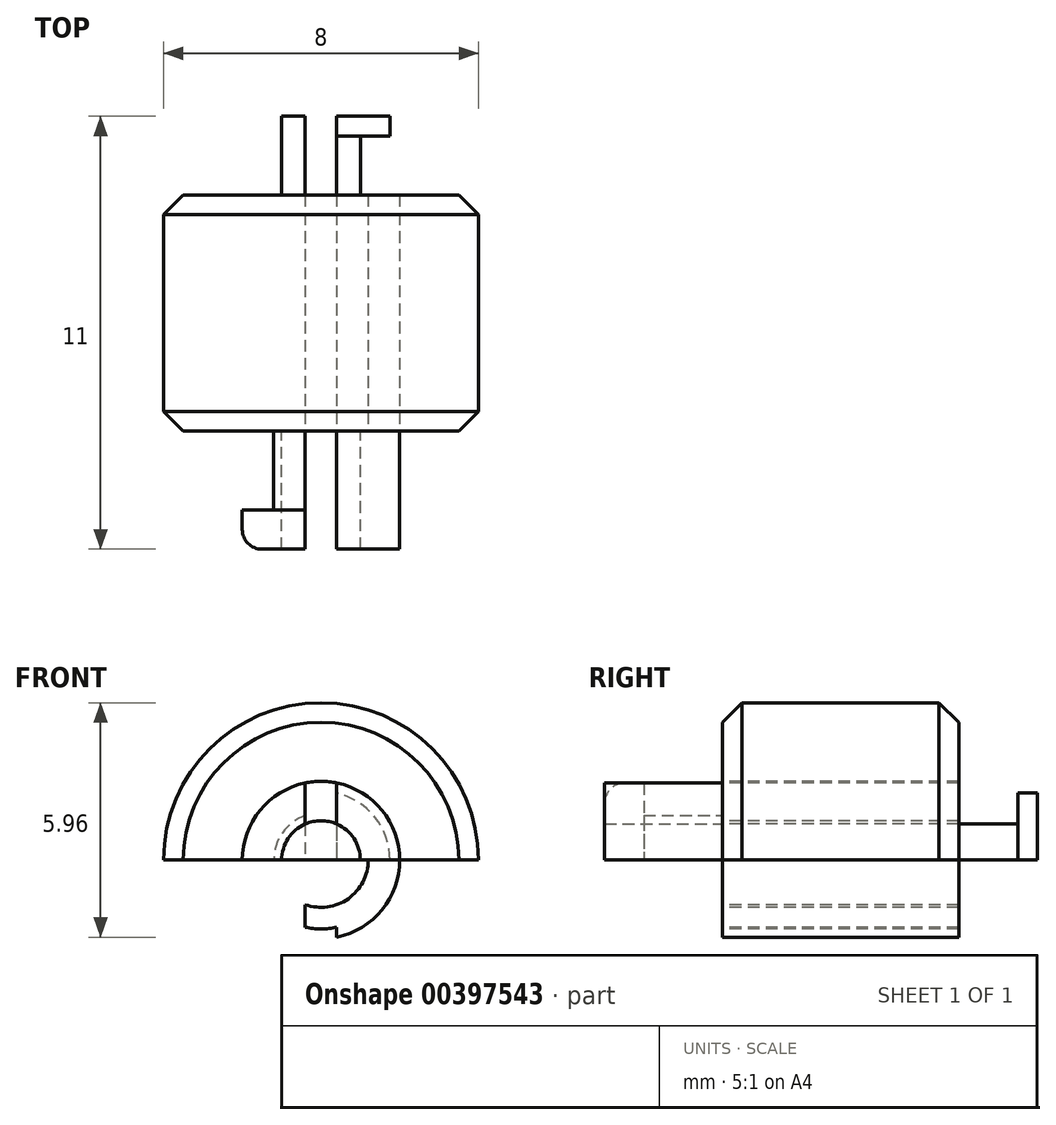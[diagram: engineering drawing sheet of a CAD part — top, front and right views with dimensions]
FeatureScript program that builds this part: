
annotation { "Feature Type Name" : "Feature", "Feature Type Description" : "" }
export const myFeature = defineFeature(function(context is Context, id is Id, definition is map)
    precondition{}
    {
        {
            var Q0;
            Q0=qCreatedBy(makeId("Front.planeOp"),FACE);
            var sketch = newSketch(context, id + "F0", { "sketchPlane" : qUnion([Q0])});
            skCircle(sketch, "E0", {"center": v(0, 0) * mm, "radius": 4 * mm});
            skLineSegment(sketch, "E1", {"start": v(-4, 0) * mm, "end": v(4, 0) * mm});
            skCircle(sketch, "E2", {"center": v(0, 0) * mm, "radius": 1.75 * mm});
            skLineSegment(sketch, "E3.bottom", {"start": v(0.4, 2) * mm, "end": v(-0.4, 2) * mm});
            skLineSegment(sketch, "E3.top", {"start": v(0.4, -2) * mm, "end": v(-0.4, -2) * mm});
            skLineSegment(sketch, "E3.left", {"start": v(0.4, 2) * mm, "end": v(0.4, -2) * mm});
            skLineSegment(sketch, "E3.right", {"start": v(-0.4, 2) * mm, "end": v(-0.4, -2) * mm});
            skCircle(sketch, "E4", {"center": v(0, 0) * mm, "radius": 2 * mm});
            skCircle(sketch, "E5", {"center": v(0, 0) * mm, "radius": 1 * mm});
            skCircle(sketch, "E6.0", {"center": v(0, 0) * mm, "radius": 1.2 * mm});
            skSolve(sketch);
        }
        {
            var Q0;
            {var subQ0=sQuery(id+"F0.wireOp",EDGE,"E1");var subQ1=sQuery(id+"F0.wireOp",EDGE,"E0");var subQ9=makeQuery(id+"F0.imprint","INTERSECT",VERTEX,{"disambiguationData":[OD(0.0)],"derivedFrom":[subQ1,subQ0]});Q0=makeQuery(id+"F0.imprint","IMPRINT",FACE,{"disambiguationData":[TD([[makeQuery(id+"F0.imprint","IMPRINT",EDGE,{"disambiguationData":[TD([[subQ9,1.0]])],"derivedFrom":subQ1}),1.0]])]});}
            var Q1;
            {var subQ0=sQuery(id+"F0.wireOp",EDGE,"E2");var subQ1=sQuery(id+"F0.wireOp",EDGE,"E1");var subQ2=makeQuery(id+"F0.imprint","INTERSECT",VERTEX,{"disambiguationData":[OD(1.0)],"derivedFrom":[subQ1,subQ0]});Q1=makeQuery(id+"F0.imprint","IMPRINT",FACE,{"disambiguationData":[TD([[makeQuery(id+"F0.imprint","IMPRINT",EDGE,{"disambiguationData":[TD([[subQ2,-1.0]])],"derivedFrom":subQ1}),1.0]])]});}
            var Q2;
            {var subQ2=sQuery(id+"F0.wireOp",EDGE,"E3.left");var subQ4=sQuery(id+"F0.wireOp",EDGE,"E2");var subQ5=makeQuery(id+"F0.imprint","INTERSECT",VERTEX,{"disambiguationData":[OD(0.0)],"derivedFrom":[subQ4,subQ2]});Q2=makeQuery(id+"F0.imprint","IMPRINT",FACE,{"disambiguationData":[TD([[makeQuery(id+"F0.imprint","IMPRINT",EDGE,{"disambiguationData":[TD([[subQ5,-1.0]])],"derivedFrom":subQ4}),-1.0]])]});}
            var Q3;
            {var subQ0=sQuery(id+"F0.wireOp",EDGE,"E2");var subQ1=sQuery(id+"F0.wireOp",EDGE,"E1");var subQ2=makeQuery(id+"F0.imprint","INTERSECT",VERTEX,{"disambiguationData":[OD(0.0)],"derivedFrom":[subQ1,subQ0]});Q3=makeQuery(id+"F0.imprint","IMPRINT",FACE,{"disambiguationData":[TD([[makeQuery(id+"F0.imprint","IMPRINT",EDGE,{"disambiguationData":[TD([[subQ2,-1.0]])],"derivedFrom":subQ1}),1.0]])]});}
            var Q4;
            {var subQ0=sQuery(id+"F0.wireOp",EDGE,"E4");var subQ1=sQuery(id+"F0.wireOp",EDGE,"E1");var subQ2=makeQuery(id+"F0.imprint","INTERSECT",VERTEX,{"disambiguationData":[OD(0.0)],"derivedFrom":[subQ1,subQ0]});Q4=makeQuery(id+"F0.imprint","IMPRINT",FACE,{"disambiguationData":[TD([[makeQuery(id+"F0.imprint","IMPRINT",EDGE,{"disambiguationData":[TD([[subQ2,-1.0]])],"derivedFrom":subQ1}),1.0]])]});}
            var Q5;
            {var subQ0=sQuery(id+"F0.wireOp",EDGE,"E3.left");var subQ1=sQuery(id+"F0.wireOp",EDGE,"E3.bottom");var subQ2=makeQuery(id+"F0.imprint","INTERSECT",VERTEX,{"derivedFrom":[subQ1,subQ0]});Q5=makeQuery(id+"F0.imprint","IMPRINT",FACE,{"disambiguationData":[TD([[makeQuery(id+"F0.imprint","IMPRINT",EDGE,{"disambiguationData":[TD([[subQ2,-1.0]])],"derivedFrom":subQ1}),1.0]])]});}
            var Q6;
            {var subQ0=sQuery(id+"F0.wireOp",EDGE,"E3.right");var subQ1=sQuery(id+"F0.wireOp",EDGE,"E3.bottom");var subQ2=makeQuery(id+"F0.imprint","INTERSECT",VERTEX,{"derivedFrom":[subQ1,subQ0]});Q6=makeQuery(id+"F0.imprint","IMPRINT",FACE,{"disambiguationData":[TD([[makeQuery(id+"F0.imprint","IMPRINT",EDGE,{"disambiguationData":[TD([[subQ2,1.0]])],"derivedFrom":subQ1}),1.0]])]});}
            var Q7;
            {var subQ0=sQuery(id+"F0.wireOp",EDGE,"E5");var subQ1=sQuery(id+"F0.wireOp",EDGE,"E1");var subQ2=makeQuery(id+"F0.imprint","INTERSECT",VERTEX,{"disambiguationData":[OD(1.0)],"derivedFrom":[subQ1,subQ0]});Q7=makeQuery(id+"F0.imprint","IMPRINT",FACE,{"disambiguationData":[TD([[makeQuery(id+"F0.imprint","IMPRINT",EDGE,{"disambiguationData":[TD([[subQ2,-1.0]])],"derivedFrom":subQ1}),1.0]])]});}
            var Q8;
            {var subQ0=sQuery(id+"F0.wireOp",EDGE,"E3.left");var subQ1=sQuery(id+"F0.wireOp",EDGE,"E2");var subQ2=makeQuery(id+"F0.imprint","INTERSECT",VERTEX,{"disambiguationData":[OD(0.0)],"derivedFrom":[subQ1,subQ0]});Q8=makeQuery(id+"F0.imprint","IMPRINT",FACE,{"disambiguationData":[TD([[makeQuery(id+"F0.imprint","IMPRINT",EDGE,{"disambiguationData":[TD([[subQ2,-1.0]])],"derivedFrom":subQ1}),1.0]])]});}
            var Q9;
            {var subQ0=sQuery(id+"F0.wireOp",EDGE,"E6.0");var subQ1=sQuery(id+"F0.wireOp",EDGE,"E1");var subQ2=makeQuery(id+"F0.imprint","INTERSECT",VERTEX,{"disambiguationData":[OD(1.0)],"derivedFrom":[subQ1,subQ0]});Q9=makeQuery(id+"F0.imprint","IMPRINT",FACE,{"disambiguationData":[TD([[makeQuery(id+"F0.imprint","IMPRINT",EDGE,{"disambiguationData":[TD([[subQ2,-1.0]])],"derivedFrom":subQ1}),1.0]])]});}
            var Q10;
            {var subQ0=sQuery(id+"F0.wireOp",EDGE,"E6.0");var subQ1=sQuery(id+"F0.wireOp",EDGE,"E3.left");var subQ2=makeQuery(id+"F0.imprint","INTERSECT",VERTEX,{"disambiguationData":[OD(0.0)],"derivedFrom":[subQ1,subQ0]});Q10=makeQuery(id+"F0.imprint","IMPRINT",FACE,{"disambiguationData":[TD([[makeQuery(id+"F0.imprint","IMPRINT",EDGE,{"disambiguationData":[TD([[subQ2,-1.0]])],"derivedFrom":subQ1}),-1.0]])]});}
            var Q11;
            {var subQ0=sQuery(id+"F0.wireOp",EDGE,"E6.0");var subQ1=sQuery(id+"F0.wireOp",EDGE,"E1");var subQ2=makeQuery(id+"F0.imprint","INTERSECT",VERTEX,{"disambiguationData":[OD(0.0)],"derivedFrom":[subQ1,subQ0]});Q11=makeQuery(id+"F0.imprint","IMPRINT",FACE,{"disambiguationData":[TD([[makeQuery(id+"F0.imprint","IMPRINT",EDGE,{"disambiguationData":[TD([[subQ2,-1.0]])],"derivedFrom":subQ1}),1.0]])]});}
            var Q12;
            {var subQ0=sQuery(id+"F0.wireOp",EDGE,"E3.left");var subQ1=sQuery(id+"F0.wireOp",EDGE,"E1");var subQ2=makeQuery(id+"F0.imprint","INTERSECT",VERTEX,{"derivedFrom":[subQ1,subQ0]});Q12=makeQuery(id+"F0.imprint","IMPRINT",FACE,{"disambiguationData":[TD([[makeQuery(id+"F0.imprint","IMPRINT",EDGE,{"disambiguationData":[TD([[subQ2,-1.0]])],"derivedFrom":subQ1}),1.0]])]});}
            var Q13;
            {var subQ0=sQuery(id+"F0.wireOp",EDGE,"E3.right");var subQ1=sQuery(id+"F0.wireOp",EDGE,"E1");var subQ2=makeQuery(id+"F0.imprint","INTERSECT",VERTEX,{"derivedFrom":[subQ1,subQ0]});Q13=makeQuery(id+"F0.imprint","IMPRINT",FACE,{"disambiguationData":[TD([[makeQuery(id+"F0.imprint","IMPRINT",EDGE,{"disambiguationData":[TD([[subQ2,-1.0]])],"derivedFrom":subQ1}),1.0]])]});}
            var Q14;
            {var subQ0=sQuery(id+"F0.wireOp",EDGE,"E5");var subQ1=sQuery(id+"F0.wireOp",EDGE,"E1");var subQ2=makeQuery(id+"F0.imprint","INTERSECT",VERTEX,{"disambiguationData":[OD(0.0)],"derivedFrom":[subQ1,subQ0]});Q14=makeQuery(id+"F0.imprint","IMPRINT",FACE,{"disambiguationData":[TD([[makeQuery(id+"F0.imprint","IMPRINT",EDGE,{"disambiguationData":[TD([[subQ2,-1.0]])],"derivedFrom":subQ1}),1.0]])]});}
            extrude(context, id + "F1", {"entities" : qUnion([Q0, Q1, Q2, Q3, Q4, Q5, Q6, Q7, Q8, Q9, Q10, Q11, Q12, Q13, Q14]), "oppositeDirection" : true, "depth" : 6 * mm});
        }
        {
            var Q0;
            {var subQ0=sQuery(id+"F0.wireOp",EDGE,"E2");var subQ1=sQuery(id+"F0.wireOp",EDGE,"E1");var subQ2=makeQuery(id+"F0.imprint","INTERSECT",VERTEX,{"disambiguationData":[OD(0.0)],"derivedFrom":[subQ1,subQ0]});Q0=makeQuery(id+"F0.imprint","IMPRINT",FACE,{"disambiguationData":[TD([[makeQuery(id+"F0.imprint","IMPRINT",EDGE,{"disambiguationData":[TD([[subQ2,-1.0]])],"derivedFrom":subQ1}),1.0]])]});}
            var Q1;
            {var subQ0=sQuery(id+"F0.wireOp",EDGE,"E5");var subQ1=sQuery(id+"F0.wireOp",EDGE,"E1");var subQ2=makeQuery(id+"F0.imprint","INTERSECT",VERTEX,{"disambiguationData":[OD(1.0)],"derivedFrom":[subQ1,subQ0]});Q1=makeQuery(id+"F0.imprint","IMPRINT",FACE,{"disambiguationData":[TD([[makeQuery(id+"F0.imprint","IMPRINT",EDGE,{"disambiguationData":[TD([[subQ2,-1.0]])],"derivedFrom":subQ1}),1.0]])]});}
            var Q2;
            {var subQ0=sQuery(id+"F0.wireOp",EDGE,"E6.0");var subQ1=sQuery(id+"F0.wireOp",EDGE,"E1");var subQ2=makeQuery(id+"F0.imprint","INTERSECT",VERTEX,{"disambiguationData":[OD(1.0)],"derivedFrom":[subQ1,subQ0]});Q2=makeQuery(id+"F0.imprint","IMPRINT",FACE,{"disambiguationData":[TD([[makeQuery(id+"F0.imprint","IMPRINT",EDGE,{"disambiguationData":[TD([[subQ2,-1.0]])],"derivedFrom":subQ1}),1.0]])]});}
            var Q3;
            {var subQ0=sQuery(id+"F0.wireOp",EDGE,"E6.0");var subQ1=sQuery(id+"F0.wireOp",EDGE,"E1");var subQ2=makeQuery(id+"F0.imprint","INTERSECT",VERTEX,{"disambiguationData":[OD(0.0)],"derivedFrom":[subQ1,subQ0]});Q3=makeQuery(id+"F0.imprint","IMPRINT",FACE,{"disambiguationData":[TD([[makeQuery(id+"F0.imprint","IMPRINT",EDGE,{"disambiguationData":[TD([[subQ2,-1.0]])],"derivedFrom":subQ1}),1.0]])]});}
            extrude(context, id + "F2", {"entities" : qUnion([Q0, Q1, Q2, Q3]), "operationType" : NewBodyOperationType.ADD, "depth" : 3 * mm});
        }
        {
            var Q0;
            {var subQ0=sQuery(id+"F0.wireOp",EDGE,"E2");var subQ1=sQuery(id+"F0.wireOp",EDGE,"E1");var subQ2=makeQuery(id+"F0.imprint","INTERSECT",VERTEX,{"disambiguationData":[OD(1.0)],"derivedFrom":[subQ1,subQ0]});Q0=makeQuery(id+"F0.imprint","IMPRINT",FACE,{"disambiguationData":[TD([[makeQuery(id+"F0.imprint","IMPRINT",EDGE,{"disambiguationData":[TD([[subQ2,-1.0]])],"derivedFrom":subQ1}),1.0]])]});}
            var Q1;
            {var subQ0=sQuery(id+"F0.wireOp",EDGE,"E4");var subQ1=sQuery(id+"F0.wireOp",EDGE,"E1");var subQ2=makeQuery(id+"F0.imprint","INTERSECT",VERTEX,{"disambiguationData":[OD(0.0)],"derivedFrom":[subQ1,subQ0]});Q1=makeQuery(id+"F0.imprint","IMPRINT",FACE,{"disambiguationData":[TD([[makeQuery(id+"F0.imprint","IMPRINT",EDGE,{"disambiguationData":[TD([[subQ2,-1.0]])],"derivedFrom":subQ1}),1.0]])]});}
            extrude(context, id + "F3", {"entities" : qUnion([Q0, Q1]), "operationType" : NewBodyOperationType.ADD, "depth" : 3 * mm, "hasSecondDirection" : true, "secondDirectionOppositeDirection" : false, "secondDirectionDepth" : 2 * mm});
        }
        {
            var Q0;
            Q0=makeQuery(id+"F1.opExtrude","CAP_EDGE",EDGE,{"disambiguationData":[OSD([sQuery(id+"F0.wireOp",EDGE,"E0")])],"isStart":true});
            var Q1;
            Q1=makeQuery(id+"F1.opExtrude","CAP_EDGE",EDGE,{"disambiguationData":[OSD([sQuery(id+"F0.wireOp",EDGE,"E0")])],"isStart":false});
            chamfer(context, id + "F4", {"entities" : qUnion([Q0, Q1]), "width" : 0.5 * mm, "tangentPropagation" : true});
        }
        {
            var Q0;
            {var subQ0=sQuery(id+"F0.wireOp",EDGE,"E3.left");var subQ1=sQuery(id+"F0.wireOp",EDGE,"E1");var subQ2=makeQuery(id+"F0.imprint","INTERSECT",VERTEX,{"derivedFrom":[subQ1,subQ0]});Q0=makeQuery(id+"F0.imprint","IMPRINT",FACE,{"disambiguationData":[TD([[makeQuery(id+"F0.imprint","IMPRINT",EDGE,{"disambiguationData":[TD([[subQ2,-1.0]])],"derivedFrom":subQ1}),1.0]])]});}
            var Q1;
            {var subQ0=sQuery(id+"F0.wireOp",EDGE,"E5");var subQ1=sQuery(id+"F0.wireOp",EDGE,"E1");var subQ2=makeQuery(id+"F0.imprint","INTERSECT",VERTEX,{"disambiguationData":[OD(0.0)],"derivedFrom":[subQ1,subQ0]});Q1=makeQuery(id+"F0.imprint","IMPRINT",FACE,{"disambiguationData":[TD([[makeQuery(id+"F0.imprint","IMPRINT",EDGE,{"disambiguationData":[TD([[subQ2,-1.0]])],"derivedFrom":subQ1}),1.0]])]});}
            extrude(context, id + "F5", {"entities" : qUnion([Q0, Q1]), "operationType" : NewBodyOperationType.ADD, "oppositeDirection" : true, "depth" : 8 * mm});
        }
        {
            var Q0;
            {var subQ0=sQuery(id+"F0.wireOp",EDGE,"E6.0");var subQ1=sQuery(id+"F0.wireOp",EDGE,"E1");var subQ2=makeQuery(id+"F0.imprint","INTERSECT",VERTEX,{"disambiguationData":[OD(0.0)],"derivedFrom":[subQ1,subQ0]});Q0=makeQuery(id+"F0.imprint","IMPRINT",FACE,{"disambiguationData":[TD([[makeQuery(id+"F0.imprint","IMPRINT",EDGE,{"disambiguationData":[TD([[subQ2,-1.0]])],"derivedFrom":subQ1}),1.0]])]});}
            var Q1;
            {var subQ0=sQuery(id+"F0.wireOp",EDGE,"E5");var subQ1=sQuery(id+"F0.wireOp",EDGE,"E1");var subQ2=makeQuery(id+"F0.imprint","INTERSECT",VERTEX,{"disambiguationData":[OD(1.0)],"derivedFrom":[subQ1,subQ0]});Q1=makeQuery(id+"F0.imprint","IMPRINT",FACE,{"disambiguationData":[TD([[makeQuery(id+"F0.imprint","IMPRINT",EDGE,{"disambiguationData":[TD([[subQ2,-1.0]])],"derivedFrom":subQ1}),1.0]])]});}
            extrude(context, id + "F6", {"entities" : qUnion([Q0, Q1]), "operationType" : NewBodyOperationType.ADD, "oppositeDirection" : true, "depth" : 8 * mm, "hasSecondDirection" : true, "secondDirectionOppositeDirection" : true, "secondDirectionDepth" : 7.5 * mm});
        }
        {
            var Q0;
            {var subQ0=sQuery(id+"F0.wireOp",EDGE,"E6.0");Q0=makeQuery(id+"F6.opExtrude","CAP_EDGE",EDGE,{"disambiguationData":[OSD([subQ0]),TDD([makeQuery(id+"F0.imprint","IMPRINT",EDGE,{"disambiguationData":[TD([[makeQuery(id+"F0.imprint","INTERSECT",VERTEX,{"disambiguationData":[OD(1.0)],"derivedFrom":[sQuery(id+"F0.wireOp",EDGE,"E1"),subQ0]}),-1.0]])],"derivedFrom":subQ0})])],"isStart":false});}
            var Q1;
            {var subQ0=sQuery(id+"F0.wireOp",EDGE,"E6.0");Q1=makeQuery(id+"F6.opExtrude","CAP_EDGE",EDGE,{"disambiguationData":[OSD([subQ0]),TDD([makeQuery(id+"F0.imprint","IMPRINT",EDGE,{"disambiguationData":[TD([[makeQuery(id+"F0.imprint","INTERSECT",VERTEX,{"disambiguationData":[OD(0.0)],"derivedFrom":[sQuery(id+"F0.wireOp",EDGE,"E1"),subQ0]}),1.0]])],"derivedFrom":subQ0})])],"isStart":false});}
            var Q2;
            {var subQ0=sQuery(id+"F0.wireOp",EDGE,"E4");Q2=makeQuery(id+"F3.opExtrude","CAP_EDGE",EDGE,{"disambiguationData":[OSD([subQ0]),TDD([makeQuery(id+"F0.imprint","IMPRINT",EDGE,{"disambiguationData":[TD([[makeQuery(id+"F0.imprint","INTERSECT",VERTEX,{"disambiguationData":[OD(1.0)],"derivedFrom":[sQuery(id+"F0.wireOp",EDGE,"E1"),subQ0]}),-1.0]])],"derivedFrom":subQ0})])],"isStart":false});}
            var Q3;
            {var subQ0=sQuery(id+"F0.wireOp",EDGE,"E4");Q3=makeQuery(id+"F3.opExtrude","CAP_EDGE",EDGE,{"disambiguationData":[OSD([subQ0]),TDD([makeQuery(id+"F0.imprint","IMPRINT",EDGE,{"disambiguationData":[TD([[makeQuery(id+"F0.imprint","INTERSECT",VERTEX,{"disambiguationData":[OD(0.0)],"derivedFrom":[sQuery(id+"F0.wireOp",EDGE,"E1"),subQ0]}),1.0]])],"derivedFrom":subQ0})])],"isStart":false});}
            fillet(context, id + "F7", {"entities" : qUnion([Q0, Q1, Q2, Q3]), "radius" : 0.5 * mm, "tangentPropagation" : true, "allowEdgeOverflow" : false});
        }
    });
